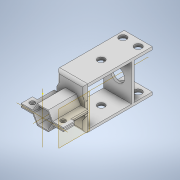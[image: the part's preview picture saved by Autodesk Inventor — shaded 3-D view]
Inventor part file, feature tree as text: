
AUTODESK INVENTOR PART (.ipt)
format: ipt  version: 2021 (Build 250183000, 183)  size: 404,992 bytes
history: native  units: mm
features: sketch x17, extrude x15, other x6, move_body x6, mirror x5, projected_geometry x4, direct_edit x3, reference x2, plane x1, fillet x1
ambient origin geometry x8: Origin, YZ Plane, XZ Plane, XY Plane, X Axis, Y Axis, Z Axis, Center Point
bodies: Solid1 (feature_tree)
feature tree (60):
  extrude  "Extrusion1"  Depth=5.0mm
  extrude  "Extrusion3"  Depth=6.9mm
  extrude  "Extrusion4"  Depth=10.0mm
  extrude  "Extrusion5"  Depth=1.0mm
  plane  "Work Plane1"
  extrude  "Extrusion6"  Depth=0.8mm
  mirror  "Mirror1"
  mirror  "Mirror2"
  extrude  "Extrusion7"  Depth=8.0mm TaperAngle=0.0deg
  mirror  "Mirror3"
  extrude  "Extrusion8"  Depth=5.0mm TaperAngle=0.0deg
  fillet  "Fillet1"  Radius=20.0mm
  extrude  "Extrusion9"  Depth=35.0mm TaperAngle=0.0deg
  extrude  "Extrusion10"  Depth=5.0mm
  sketch  "Sketch12"  dims[d31=35.0mm d32=0.0mm d33=3.0mm]
  sketch  "Sketch14"  dims[d34=3.0mm d35=10.0mm d36=0.0mm]
  extrude  "Extrusion13"  Depth=35.0mm
  extrude  "Extrusion14"  Depth=10.0mm TaperAngle=0.0deg
  extrude  "Extrusion15"  Depth=33.0mm TaperAngle=0.0deg
  mirror  "Mirror4"
  extrude  "Extrusion16"  Depth=20.0mm
  extrude  "Extrusion17"  TaperAngle=0.0deg  [1 undecoded]
  extrude  "Extrusion18"  Depth=1.0mm TaperAngle=0.0deg
  mirror  "Mirror5"
  direct_edit  "Direct Edit1"
  direct_edit  "Direct Edit2"
  direct_edit  "Direct Edit3"
  sketch  "Sketch1"  dims[d0=6.9mm d1=5.0mm]
  sketch  "Sketch4"  dims[d2=20.0mm d3=0.0mm d7=6.9mm]
  sketch  "Sketch5"  dims[d8=10.0mm d9=0.0mm d10=10.0mm]
  sketch  "Sketch6"  dims[d11=10.0mm d12=0.0mm d13=1.0mm]
  sketch  "Sketch7"  dims[d14=10.0mm d15=0.0mm d16=0.8mm]
  sketch  "Sketch8"  dims[d17=8.0mm d18=8.0mm d19=1.0mm d20=0.0mm d21=0.0mm]
  sketch  "Sketch9"  dims[d22=3.5mm d23=5.0mm d24=0.0mm d25=20.0mm]
  sketch  "Sketch10"  dims[d26=30.0mm d27=35.0mm d28=0.0mm]
  sketch  "Sketch11"  dims[d29=2.0mm d30=5.0mm]
  sketch  "Sketch16"  dims[d43=33.0mm d44=0.0mm d45=3.0mm d46=0.0mm]
  reference  "Reference2"
  reference  "Reference3"
  sketch  "Sketch17"  dims[d47=20.0mm d48=0.0mm d49=3.5mm]
  projected_geometry  "Projected Loop1"
  projected_geometry  "Projected Loop2"
  sketch  "Sketch18"  dims[d50=10.0mm d51=0.0mm d52=0.0mm d53=0.0mm]
  projected_geometry  "Projected Loop3"
  sketch  "Sketch19"  dims[d54=42.25mm d55=0.0mm d56=0.0mm d57=0.0mm d58=1.0mm]
  sketch  "Sketch20"  dims[d59=0.0mm d60=0.0mm d61=-1.0mm]
  sketch  "Sketch21"  dims[d62=0.0mm d63=0.0mm d64=-1.0mm d65=0.0mm d66=0.0mm d67=-1.0mm d68=-1.0mm d69=0.0mm d70=0.0mm d71=-5.75mm d72=0.0mm d73=0.0mm d74=-5.0mm d75=-1.0mm]
  projected_geometry  "Projected Loop4"
  parser-record x1  (decoder bookkeeping rows leaked as tree rows — omitted from the tree; the rows remain in map.json)
  other  "whole_assembly.iam"
  other  "Part3:1"
  other  "tool_holder:1"
  move_body  "Move1"
  move_body  "Move2"
  move_body  "Move3"
  move_body  "Move4"
  other  "Size1"
  move_body  "Move5"
  move_body  "Move6"
  other  "Size2"
note: 1 required parameter value undecoded (feature->parameter linkage not recoverable at this tier; creation-order binding heuristic only, values carry confidence <= 0.55)
note: 1 file-system path scrubbed to <path> (originals preserved in map.json)
